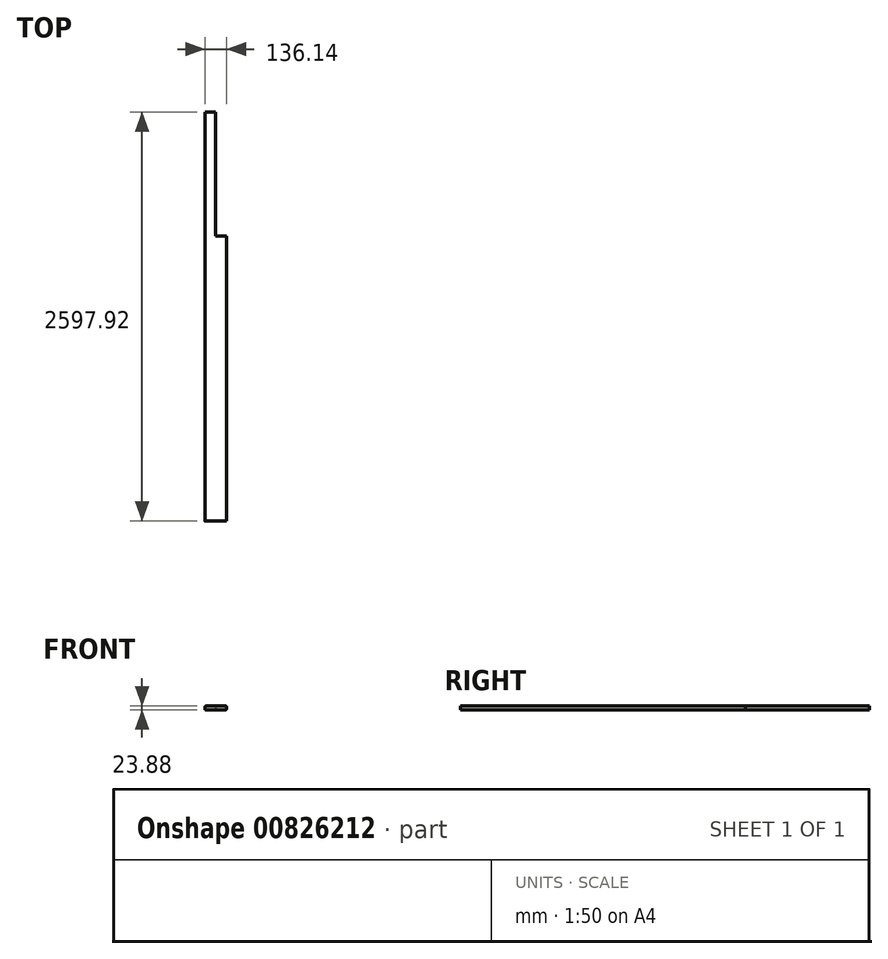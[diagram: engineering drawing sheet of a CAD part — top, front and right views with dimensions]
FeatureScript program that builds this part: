
annotation { "Feature Type Name" : "Feature", "Feature Type Description" : "" }
export const myFeature = defineFeature(function(context is Context, id is Id, definition is map)
    precondition{}
    {
        {
            var Q0;
            Q0=qCreatedBy(makeId("Front.planeOp"),FACE);
            var sketch = newSketch(context, id + "F0", { "sketchPlane" : qUnion([Q0])});
            skLineSegment(sketch, "E0.bottom", {"start": v(-63.25, 11.94) * mm, "end": v(63.25, 11.94) * mm});
            skLineSegment(sketch, "E0.top", {"start": v(-63.25, -11.94) * mm, "end": v(63.25, -11.94) * mm});
            skLineSegment(sketch, "E0.left", {"start": v(-68.07, 7.11) * mm, "end": v(-68.07, -7.11) * mm});
            skLineSegment(sketch, "E0.right", {"start": v(68.07, 7.11) * mm, "end": v(68.07, -7.11) * mm});
            skPoint(sketch, "E0.middle", {"position": v(0, 0) * mm});
            skPoint(sketch, "E1.visualSharp", {"position": v(-68.07, 11.94) * mm});
            skArc(sketch, "E1.filletArc", {"start": v(-63.25, 11.94) * mm, "mid": v(-66.66, 10.52) * mm, "end": v(-68.07, 7.11) * mm});
            skPoint(sketch, "E2.visualSharp", {"position": v(68.07, 11.94) * mm});
            skArc(sketch, "E2.filletArc", {"start": v(68.07, 7.11) * mm, "mid": v(66.66, 10.52) * mm, "end": v(63.25, 11.94) * mm});
            skPoint(sketch, "E3.visualSharp", {"position": v(68.07, -11.94) * mm});
            skArc(sketch, "E3.filletArc", {"start": v(63.25, -11.94) * mm, "mid": v(66.66, -10.52) * mm, "end": v(68.07, -7.11) * mm});
            skPoint(sketch, "E4.visualSharp", {"position": v(-68.07, -11.94) * mm});
            skArc(sketch, "E4.filletArc", {"start": v(-68.07, -7.11) * mm, "mid": v(-66.66, -10.52) * mm, "end": v(-63.25, -11.94) * mm});
            skSolve(sketch);
        }
        {
            var Q0;
            Q0=makeQuery(id+"F0.imprint","IMPRINT",FACE,{"disambiguationData":[TD([[makeQuery(id+"F0.imprint","IMPRINT",EDGE,{"derivedFrom":sQuery(id+"F0.wireOp",EDGE,"E0.bottom")}),-1.0]])]});
            extrude(context, id + "F1", {"entities" : qUnion([Q0]), "endBound" : BoundingType.SYMMETRIC, "depth" : 2597.9 * mm, "offsetDistance" : 25.4 * mm});
        }
        {
            var Q0;
            Q0=makeQuery(id+"F1.opExtrude","SWEPT_FACE",FACE,{"disambiguationData":[OSD([sQuery(id+"F0.wireOp",EDGE,"E0.bottom")])]});
            var sketch = newSketch(context, id + "F2", { "sketchPlane" : qUnion([Q0])});
            skLineSegment(sketch, "E5.bottom", {"start": v(113.87, 1440.77) * mm, "end": v(0, 1440.77) * mm});
            skLineSegment(sketch, "E5.top", {"start": v(113.87, 511.56) * mm, "end": v(0, 511.56) * mm});
            skLineSegment(sketch, "E5.left", {"start": v(113.87, 1440.77) * mm, "end": v(113.87, 511.56) * mm});
            skLineSegment(sketch, "E5.right", {"start": v(0, 1440.77) * mm, "end": v(0, 511.56) * mm});
            skSolve(sketch);
        }
        {
            var Q0;
            Q0=qSketchRegion(id+"F2",true);
            extrude(context, id + "F3", {"entities" : qUnion([Q0]), "operationType" : NewBodyOperationType.REMOVE, "endBound" : BoundingType.THROUGH_ALL, "oppositeDirection" : true, "depth" : 25.4 * mm, "offsetDistance" : 25.4 * mm});
        }
    });
